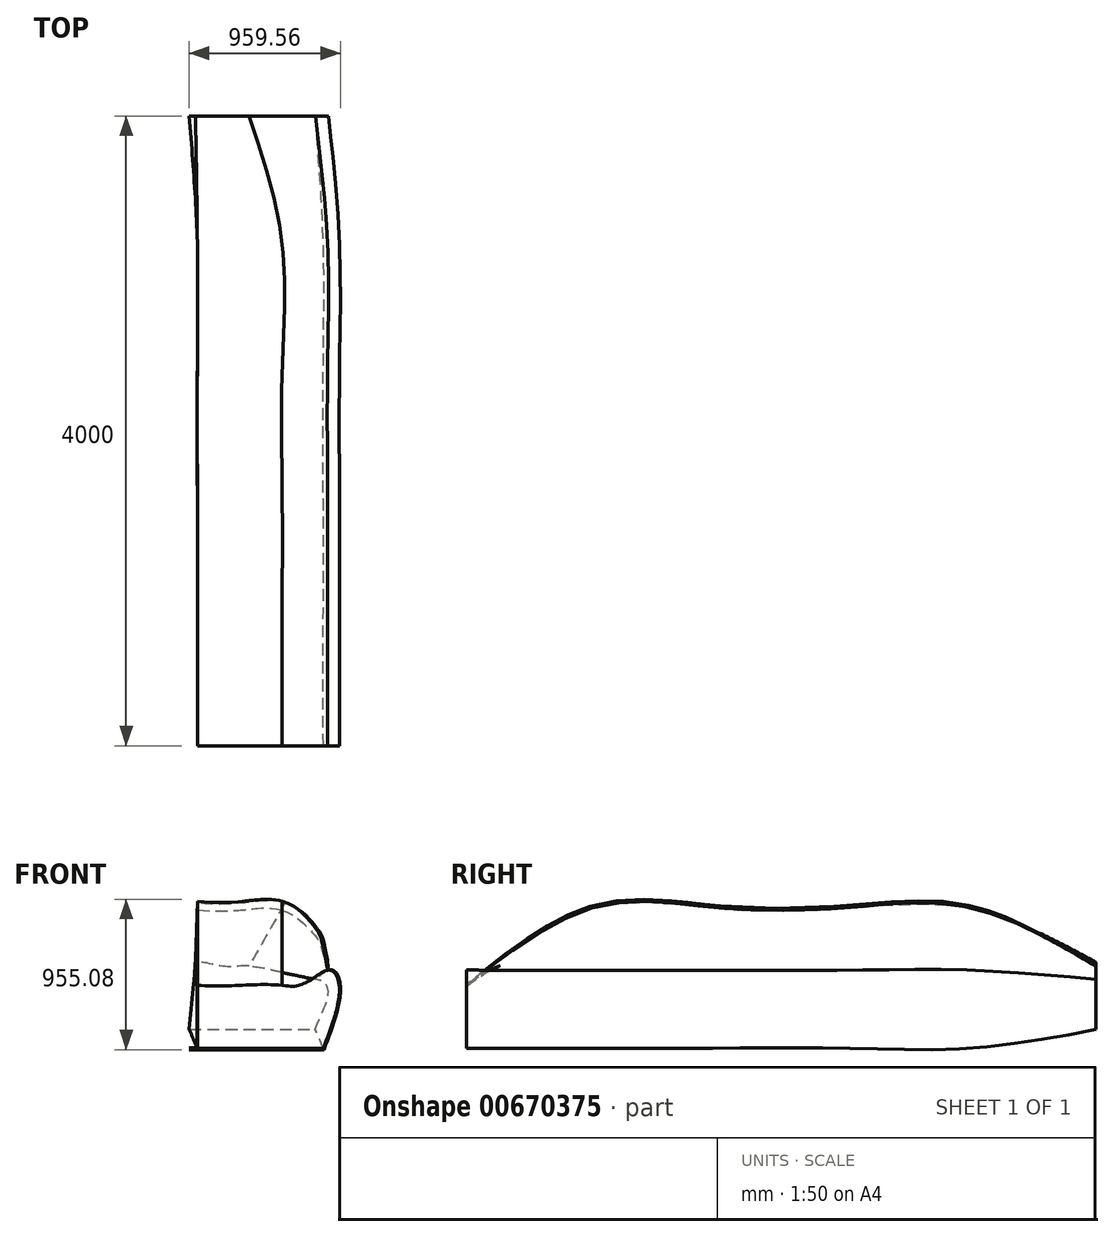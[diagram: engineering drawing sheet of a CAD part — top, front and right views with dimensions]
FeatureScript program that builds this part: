
annotation { "Feature Type Name" : "Feature", "Feature Type Description" : "" }
export const myFeature = defineFeature(function(context is Context, id is Id, definition is map)
    precondition{}
    {
        {
            var Q0;
            Q0=qCreatedBy(makeId("Front.planeOp"),FACE);
            var Q1;
            Q1 = qBodyType(qCreatedBy(id + "Fli9hLaPclbL4vP_0" ,EDGE), BodyType.WIRE);
            cPlane(context, id + "F0", {"entities" : qUnion([Q0, Q1]), "cplaneType" : CPlaneType.OFFSET, "offset" : 800 * mm, "width" : 150 * mm, "height" : 150 * mm});
        }
        {
            var Q0;
            Q0=qCreatedBy(id+"F0.planeOp",FACE);
            cPlane(context, id + "F1", {"entities" : qUnion([Q0]), "cplaneType" : CPlaneType.OFFSET, "offset" : 800 * mm, "width" : 150 * mm, "height" : 150 * mm});
        }
        {
            var Q0;
            Q0=qCreatedBy(id+"F1.planeOp",FACE);
            cPlane(context, id + "F2", {"entities" : qUnion([Q0]), "cplaneType" : CPlaneType.OFFSET, "offset" : 800 * mm, "width" : 150 * mm, "height" : 150 * mm});
        }
        {
            var Q0;
            Q0=qCreatedBy(id+"F2.planeOp",FACE);
            cPlane(context, id + "F3", {"entities" : qUnion([Q0]), "cplaneType" : CPlaneType.OFFSET, "offset" : 800 * mm, "width" : 150 * mm, "height" : 150 * mm});
        }
        {
            var Q0;
            Q0=qCreatedBy(id+"F3.planeOp",FACE);
            cPlane(context, id + "F4", {"entities" : qUnion([Q0]), "cplaneType" : CPlaneType.OFFSET, "offset" : 800 * mm, "width" : 150 * mm, "height" : 150 * mm});
        }
        {
            var Q0;
            Q0=qCreatedBy(id+"F4.planeOp",FACE);
            cPlane(context, id + "F5", {"entities" : qUnion([Q0]), "cplaneType" : CPlaneType.OFFSET, "offset" : 800 * mm, "width" : 150 * mm, "height" : 150 * mm});
        }
        {
            var Q0;
            Q0=qCreatedBy(id+"F1.planeOp",FACE);
            var sketch = newSketch(context, id + "F6", { "sketchPlane" : qUnion([Q0])});
            skLineSegment(sketch, "E0", {"start": v(-451.75, -464.92) * mm, "end": v(348.25, -464.92) * mm});
            skFitSpline(sketch, "E1", {"points": [v(348.25, -464.92) * mm, v(451.06, -91.84) * mm, v(412.01, 21.8) * mm, v(375.05, 30.62) * mm], "startDerivative": vector(302.42, 775.01) * mm, "endDerivative": vector(-188.7, 64.87) * mm});
            skFitSpline(sketch, "E2", {"points": [v(375.05, 30.62) * mm, v(330.26, 210.65) * mm, v(294.75, 269.25) * mm, v(225.5, 345.6) * mm, v(87, 426.75) * mm], "startDerivative": vector(-67.69, 319.7) * mm, "endDerivative": vector(-527.96, 92.23) * mm});
            skFitSpline(sketch, "E3", {"points": [v(87, 426.75) * mm, v(-170.02, 426.75) * mm, v(-451.75, 426.75) * mm], "startDerivative": vector(-510.39, 152.53) * mm, "endDerivative": vector(-580.89, 51.06) * mm});
            skLineSegment(sketch, "E4", {"start": v(-451.75, 426.75) * mm, "end": v(-451.75, -464.92) * mm});
            skSolve(sketch);
        }
        {
            var Q0;
            Q0=qCreatedBy(id+"F2.planeOp",FACE);
            var sketch = newSketch(context, id + "F7", { "sketchPlane" : qUnion([Q0])});
            skLineSegment(sketch, "E5", {"start": v(-451.75, -464.92) * mm, "end": v(348.25, -464.92) * mm});
            skFitSpline(sketch, "E6", {"points": [v(348.25, -464.92) * mm, v(451.06, -91.84) * mm, v(412.01, 21.8) * mm, v(375.05, 30.62) * mm], "startDerivative": vector(302.42, 775.01) * mm, "endDerivative": vector(-188.7, 64.87) * mm});
            skFitSpline(sketch, "E7", {"points": [v(375.05, 30.62) * mm, v(330.26, 210.65) * mm, v(294.75, 269.25) * mm, v(225.5, 345.6) * mm, v(87, 426.75) * mm], "startDerivative": vector(-67.69, 319.7) * mm, "endDerivative": vector(-527.96, 92.23) * mm});
            skFitSpline(sketch, "E8", {"points": [v(87, 426.75) * mm, v(-170.02, 426.75) * mm, v(-451.75, 426.75) * mm], "startDerivative": vector(-510.39, 152.53) * mm, "endDerivative": vector(-580.89, 51.06) * mm});
            skLineSegment(sketch, "E9", {"start": v(-451.75, 426.75) * mm, "end": v(-451.75, -464.92) * mm});
            skSolve(sketch);
        }
        {
            var Q0;
            Q0=qCreatedBy(id+"F3.planeOp",FACE);
            var sketch = newSketch(context, id + "F8", { "sketchPlane" : qUnion([Q0])});
            skLineSegment(sketch, "E10", {"start": v(-451.75, -464.92) * mm, "end": v(348.25, -464.92) * mm});
            skFitSpline(sketch, "E11", {"points": [v(348.25, -464.92) * mm, v(451.06, -91.84) * mm, v(412.01, 21.8) * mm, v(375.05, 30.62) * mm], "startDerivative": vector(302.42, 775.01) * mm, "endDerivative": vector(-188.7, 64.87) * mm});
            skFitSpline(sketch, "E12", {"points": [v(375.05, 30.62) * mm, v(330.26, 210.65) * mm, v(294.75, 269.25) * mm, v(225.5, 345.6) * mm, v(87, 426.75) * mm], "startDerivative": vector(-67.69, 319.7) * mm, "endDerivative": vector(-527.96, 92.23) * mm});
            skFitSpline(sketch, "E13", {"points": [v(87, 426.75) * mm, v(-170.02, 426.75) * mm, v(-451.75, 426.75) * mm], "startDerivative": vector(-510.39, 152.53) * mm, "endDerivative": vector(-580.89, 51.06) * mm});
            skLineSegment(sketch, "E14", {"start": v(-451.75, 426.75) * mm, "end": v(-451.75, -464.92) * mm});
            skSolve(sketch);
        }
        {
            var Q0;
            Q0=qCreatedBy(id+"F4.planeOp",FACE);
            var sketch = newSketch(context, id + "F9", { "sketchPlane" : qUnion([Q0])});
            skLineSegment(sketch, "E15", {"start": v(-451.75, -464.92) * mm, "end": v(348.25, -464.92) * mm});
            skFitSpline(sketch, "E16", {"points": [v(348.25, -464.92) * mm, v(451.06, -91.84) * mm, v(412.01, 21.8) * mm, v(375.05, 30.62) * mm], "startDerivative": vector(302.42, 775.01) * mm, "endDerivative": vector(-188.7, 64.87) * mm});
            skFitSpline(sketch, "E17", {"points": [v(375.05, 30.62) * mm, v(330.26, 210.65) * mm, v(294.75, 269.25) * mm, v(225.5, 345.6) * mm, v(87, 426.75) * mm], "startDerivative": vector(-67.69, 319.7) * mm, "endDerivative": vector(-527.96, 92.23) * mm});
            skFitSpline(sketch, "E18", {"points": [v(87, 426.75) * mm, v(-170.02, 426.75) * mm, v(-451.75, 426.75) * mm], "startDerivative": vector(-510.39, 152.53) * mm, "endDerivative": vector(-580.89, 51.06) * mm});
            skLineSegment(sketch, "E19", {"start": v(-451.75, 426.75) * mm, "end": v(-451.75, -464.92) * mm});
            skSolve(sketch);
        }
        {
            var Q0;
            Q0=qCreatedBy(id+"F5.planeOp",FACE);
            var sketch = newSketch(context, id + "F10", { "sketchPlane" : qUnion([Q0])});
            skLineSegment(sketch, "E20", {"start": v(-451.75, -464.92) * mm, "end": v(348.25, -464.92) * mm});
            skFitSpline(sketch, "E21", {"points": [v(348.25, -464.92) * mm, v(451.06, -91.84) * mm, v(412.01, 21.8) * mm, v(375.05, 30.62) * mm], "startDerivative": vector(302.42, 775.01) * mm, "endDerivative": vector(-245.94, -32.76) * mm});
            skFitSpline(sketch, "E22", {"points": [v(375.05, 30.62) * mm, v(296, -13.6) * mm, v(241.8, -46.46) * mm, v(182.8, -68.23) * mm, v(87, -64.92) * mm], "startDerivative": vector(-333.88, -51.28) * mm, "endDerivative": vector(-527.96, 92.23) * mm});
            skFitSpline(sketch, "E23", {"points": [v(87, -64.92) * mm, v(-170.02, -64.92) * mm, v(-451.75, -64.92) * mm], "startDerivative": vector(-534.24, 43.68) * mm, "endDerivative": vector(-580.89, 51.06) * mm});
            skLineSegment(sketch, "E24", {"start": v(-451.75, -64.92) * mm, "end": v(-451.75, -464.92) * mm});
            skSolve(sketch);
        }
        {
            var Q0;
            Q0=qCreatedBy(id+"F0.planeOp",FACE);
            var sketch = newSketch(context, id + "F11", { "sketchPlane" : qUnion([Q0])});
            skLineSegment(sketch, "E25", {"start": v(-502.8, -346.78) * mm, "end": v(297.2, -346.78) * mm});
            skFitSpline(sketch, "E26", {"points": [v(297.2, -346.78) * mm, v(379.15, -93.75) * mm, v(339.83, -38.46) * mm, v(298.1, -26.88) * mm], "startDerivative": vector(302.42, 775.01) * mm, "endDerivative": vector(-188.7, 64.87) * mm});
            skFitSpline(sketch, "E27", {"points": [v(298.1, -26.88) * mm, v(106.04, 12.2) * mm, v(29.64, 28.48) * mm, v(0, 35.9) * mm, v(-123.44, 56.66) * mm], "startDerivative": vector(-591.99, 97.55) * mm, "endDerivative": vector(-527.96, 92.23) * mm});
            skFitSpline(sketch, "E28", {"points": [v(-123.44, 56.66) * mm, v(-303.44, 56.66) * mm, v(-463.76, 56.66) * mm], "startDerivative": vector(-316.76, 28.58) * mm, "endDerivative": vector(-88.28, -284.52) * mm});
            skLineSegment(sketch, "E29", {"start": v(-463.76, 56.66) * mm, "end": v(-502.8, -346.78) * mm});
            skSolve(sketch);
        }
        {
            var Q0;
            Q0=makeQuery(id+"F10.imprint","IMPRINT",FACE,{"disambiguationData":[TD([[makeQuery(id+"F10.imprint","IMPRINT",EDGE,{"derivedFrom":sQuery(id+"F10.wireOp",EDGE,"E20")}),1.0]])]});
            var Q1;
            Q1=makeQuery(id+"F9.imprint","IMPRINT",FACE,{"disambiguationData":[TD([[makeQuery(id+"F9.imprint","IMPRINT",EDGE,{"derivedFrom":sQuery(id+"F9.wireOp",EDGE,"E15")}),1.0]])]});
            var Q2;
            Q2=makeQuery(id+"F8.imprint","IMPRINT",FACE,{"disambiguationData":[TD([[makeQuery(id+"F8.imprint","IMPRINT",EDGE,{"derivedFrom":sQuery(id+"F8.wireOp",EDGE,"E10")}),1.0]])]});
            var Q3;
            Q3=makeQuery(id+"F7.imprint","IMPRINT",FACE,{"disambiguationData":[TD([[makeQuery(id+"F7.imprint","IMPRINT",EDGE,{"derivedFrom":sQuery(id+"F7.wireOp",EDGE,"E5")}),1.0]])]});
            var Q4;
            Q4=makeQuery(id+"F6.imprint","IMPRINT",FACE,{"disambiguationData":[TD([[makeQuery(id+"F6.imprint","IMPRINT",EDGE,{"derivedFrom":sQuery(id+"F6.wireOp",EDGE,"E0")}),1.0]])]});
            var Q5;
            Q5=makeQuery(id+"F11.imprint","IMPRINT",FACE,{"disambiguationData":[TD([[makeQuery(id+"F11.imprint","IMPRINT",EDGE,{"derivedFrom":sQuery(id+"F11.wireOp",EDGE,"E25")}),1.0]])]});
            loft(context, id + "F12", {"sheetProfilesArray" : [{ "sheetProfileEntities" : qUnion([Q0]) }, { "sheetProfileEntities" : qUnion([Q1]) }, { "sheetProfileEntities" : qUnion([Q2]) }, { "sheetProfileEntities" : qUnion([Q3]) }, { "sheetProfileEntities" : qUnion([Q4]) }, { "sheetProfileEntities" : qUnion([Q5]) }]});
        }
        {
            var Q0;
            Q0=makeQuery(id+"F12.opLoft","CAP_FACE",FACE,{"disambiguationData":[OSD([makeQuery(id+"F11.imprint","IMPRINT",FACE,{"disambiguationData":[TD([[makeQuery(id+"F11.imprint","IMPRINT",EDGE,{"derivedFrom":sQuery(id+"F11.wireOp",EDGE,"E25")}),1.0]])]})])],"isStart":true});
            cPlane(context, id + "F13", {"entities" : qUnion([Q0]), "cplaneType" : CPlaneType.OFFSET, "offset" : 100 * mm, "width" : 150 * mm, "height" : 150 * mm});
        }
    });
